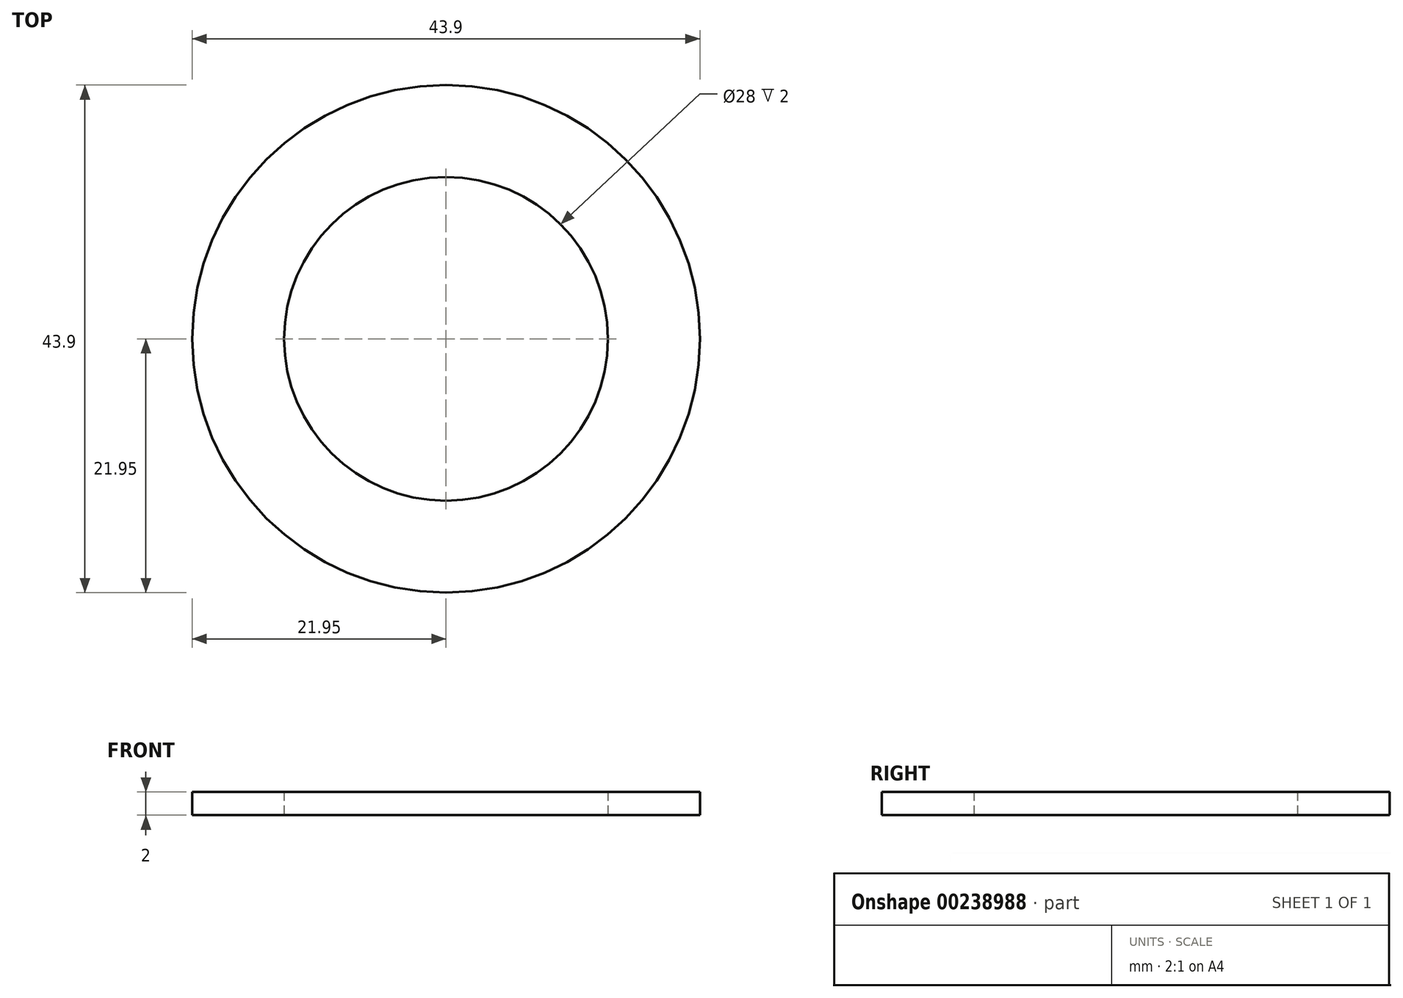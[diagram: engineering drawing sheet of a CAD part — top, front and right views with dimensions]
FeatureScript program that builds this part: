
annotation { "Feature Type Name" : "Feature", "Feature Type Description" : "" }
export const myFeature = defineFeature(function(context is Context, id is Id, definition is map)
    precondition{}
    {
        {
            var Q0;
            Q0=qCreatedBy(makeId("Top.planeOp"),FACE);
            var sketch = newSketch(context, id + "F0", { "sketchPlane" : qUnion([Q0])});
            skCircle(sketch, "E0", {"center": v(0, 0) * mm, "radius": 21.95 * mm});
            skCircle(sketch, "E1", {"center": v(0, 0) * mm, "radius": 14 * mm});
            skSolve(sketch);
        }
        {
            var Q0;
            Q0 = qSketchRegion(id + "F0", true);
            extrude(context, id + "F1", {"entities" : qUnion([Q0]), "depth" : 2 * mm});
        }
    });
